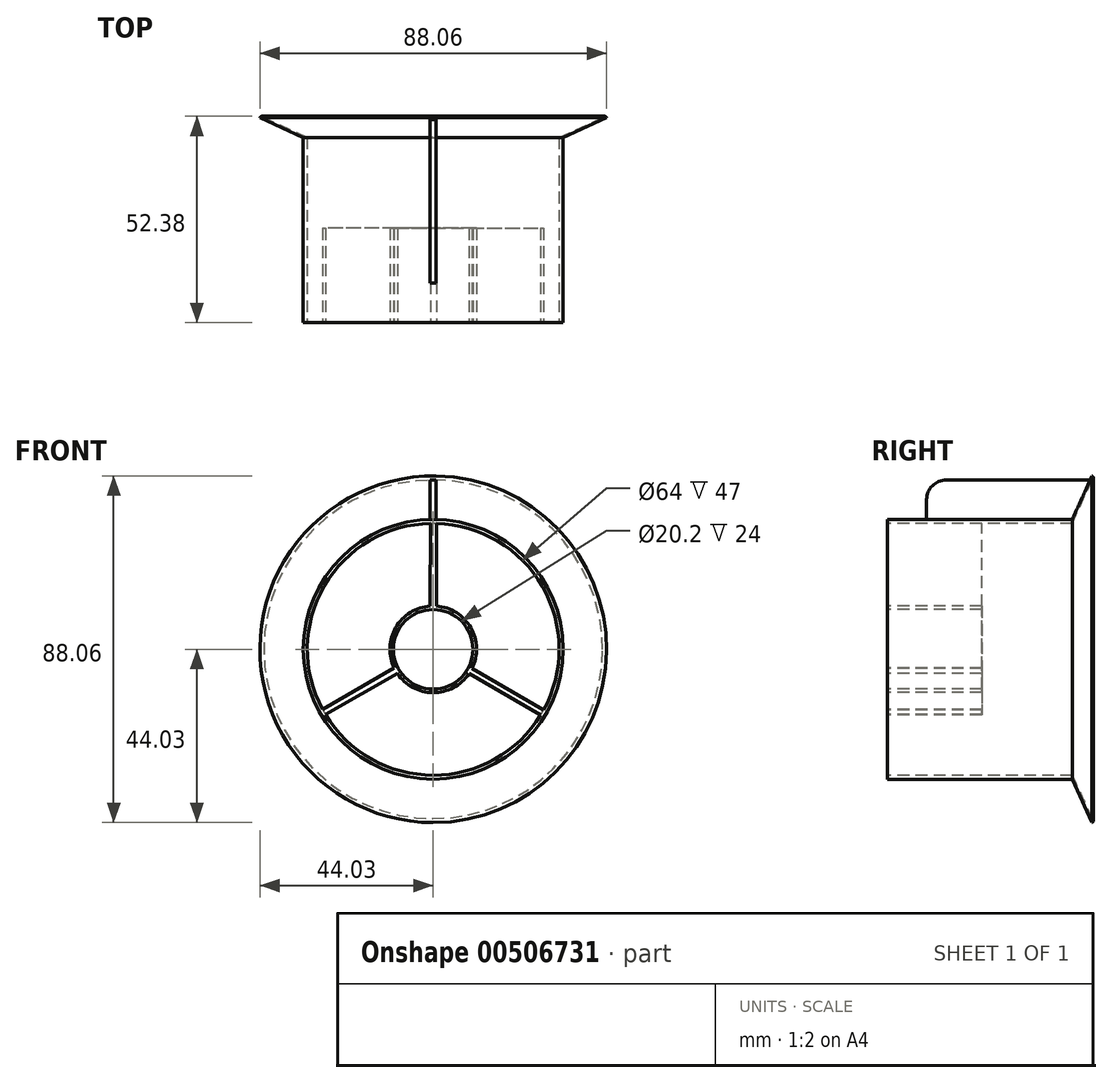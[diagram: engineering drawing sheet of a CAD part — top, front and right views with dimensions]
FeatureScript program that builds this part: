
annotation { "Feature Type Name" : "Feature", "Feature Type Description" : "" }
export const myFeature = defineFeature(function(context is Context, id is Id, definition is map)
    precondition{}
    {
        {
            var Q0;
            Q0=qCreatedBy(makeId("Front.planeOp"),FACE);
            var sketch = newSketch(context, id + "F0", { "sketchPlane" : qUnion([Q0])});
            skCircle(sketch, "E0", {"center": v(0, 0) * mm, "radius": 32 * mm});
            skCircle(sketch, "E1", {"center": v(0, 0) * mm, "radius": 33 * mm});
            skCircle(sketch, "E2", {"center": v(0, 0) * mm, "radius": 10.1 * mm});
            skCircle(sketch, "E3", {"center": v(0, 0) * mm, "radius": 11 * mm});
            skPoint(sketch, "E4.center", {"position": v(0, 0.01) * mm});
            skLineSegment(sketch, "E5.trimOffspring", {"start": v(-0.76, 10.07) * mm, "end": v(-0.65, 33) * mm});
            skLineSegment(sketch, "E6.trimOffspring", {"start": v(0.82, 10.07) * mm, "end": v(0.82, 32.99) * mm});
            skCircle(sketch, "E7", {"center": v(0, 0.01) * mm, "radius": 44 * mm});
            skCircle(sketch, "E8", {"center": v(0, 0.01) * mm, "radius": 3.42 * mm});
            skCircle(sketch, "E9", {"center": v(0, 0.01) * mm, "radius": 43 * mm});
            skLineSegment(sketch, "E10.1.0", {"start": v(-9.13, -4.32) * mm, "end": v(-28.98, -15.78) * mm});
            skLineSegment(sketch, "E10.1.1", {"start": v(-8.34, -5.7) * mm, "end": v(-28.25, -17.06) * mm});
            skLineSegment(sketch, "E10.2.0", {"start": v(8.3, -5.74) * mm, "end": v(28.16, -17.2) * mm});
            skLineSegment(sketch, "E10.2.1", {"start": v(9.1, -4.38) * mm, "end": v(28.9, -15.93) * mm});
            skSolve(sketch);
        }
        {
            var Q0;
            Q0=makeQuery(id+"F0.imprint","IMPRINT",FACE,{"disambiguationData":[TD([[makeQuery(id+"F0.imprint","IMPRINT",EDGE,{"derivedFrom":sQuery(id+"F0.wireOp",EDGE,"E1")}),1.0]])]});
            extrude(context, id + "F1", {"entities" : qUnion([Q0]), "oppositeDirection" : true, "depth" : 47 * mm, "offsetDistance" : 25 * mm});
        }
        {
            var Q0;
            Q0=qCreatedBy(makeId("Right.planeOp"),FACE);
            var sketch = newSketch(context, id + "F2", { "sketchPlane" : qUnion([Q0])});
            skLineSegment(sketch, "E11.0", {"start": v(47, 32) * mm, "end": v(47, 32) * mm});
            skLineSegment(sketch, "E11.1", {"start": v(47, -33) * mm, "end": v(47, 33) * mm});
            skLineSegment(sketch, "E12.0", {"start": v(0, -42.99) * mm, "end": v(0, 43.01) * mm});
            skLineSegment(sketch, "E12.1", {"start": v(0, -43.99) * mm, "end": v(0, 44.01) * mm});
            skLineSegment(sketch, "E13", {"start": v(47, 32) * mm, "end": v(47, 32.39) * mm});
            skLineSegment(sketch, "E14", {"start": v(47, 32) * mm, "end": v(52, 43.02) * mm});
            skLineSegment(sketch, "E15", {"start": v(47, 33) * mm, "end": v(52, 44.03) * mm});
            skArc(sketch, "E16", {"start": v(52, 43.02) * mm, "mid": v(52.38, 43.52) * mm, "end": v(52, 44.03) * mm});
            skLineSegment(sketch, "E17", {"start": v(47, 32) * mm, "end": v(47, 33) * mm});
            skLineSegment(sketch, "E18", {"start": v(27.15, 0) * mm, "end": v(34.99, 0) * mm, "construction": true});
            skLineSegment(sketch, "E19", {"start": v(47, 33) * mm, "end": v(42.98, 33) * mm, "construction": true});
            skSolve(sketch);
        }
        {
            var Q0;
            {var subQ0=sQuery(id+"F2.wireOp",EDGE,"E14");Q0=makeQuery(id+"F2.imprint","IMPRINT",FACE,{"disambiguationData":[TD([[makeQuery(id+"F2.imprint","IMPRINT",EDGE,{"derivedFrom":subQ0}),1.0]])]});}
            var Q1;
            Q1=sQuery(id+"F2.wireOp",EDGE,"E18");
            revolve(context, id + "F3", {"operationType" : NewBodyOperationType.ADD, "entities" : qUnion([Q0]), "axis" : qUnion([Q1]), "revolveType" : RevolveType.FULL});
        }
        {
            var Q0;
            {var subQ0=sQuery(id+"F0.wireOp",EDGE,"E0");Q0=makeQuery(id+"FlOwrdUnQid0o9V_1.boolean.opBoolean","MERGE",FACE,{"derivedFrom":[makeQuery(id+"F1.opExtrude","CAP_FACE",FACE,{"disambiguationData":[OSD([subQ0,sQuery(id+"F0.wireOp",EDGE,"E1"),sQuery(id+"F0.wireOp",EDGE,"09d8qYk8-wVlR-Syt2-LU9I-Puvoe7KKkESJ")])],"isStart":true}),makeQuery(id+"FlOwrdUnQid0o9V_1.opExtrude","CAP_FACE",FACE,{"disambiguationData":[OSD([subQ0,sQuery(id+"F0.wireOp",EDGE,"a5a1febd-64e9-4a83-98ac-cafd24b6d020.1.0"),sQuery(id+"F0.wireOp",EDGE,"a5a1febd-64e9-4a83-98ac-cafd24b6d020.1.1"),sQuery(id+"F0.wireOp",EDGE,"a5a1febd-64e9-4a83-98ac-cafd24b6d020.1.2")])],"isStart":true}),makeQuery(id+"FlOwrdUnQid0o9V_1.opExtrude","CAP_FACE",FACE,{"disambiguationData":[OSD([subQ0,sQuery(id+"F0.wireOp",EDGE,"a5a1febd-64e9-4a83-98ac-cafd24b6d020.2.0"),sQuery(id+"F0.wireOp",EDGE,"a5a1febd-64e9-4a83-98ac-cafd24b6d020.2.1"),sQuery(id+"F0.wireOp",EDGE,"a5a1febd-64e9-4a83-98ac-cafd24b6d020.2.2")])],"isStart":true})]});}
            cPlane(context, id + "F4", {"entities" : qUnion([Q0]), "cplaneType" : CPlaneType.OFFSET, "offset" : 10 * mm, "oppositeDirection" : true, "width" : 150 * mm, "height" : 150 * mm});
        }
        {
            var Q0;
            Q0=qCreatedBy(id+"F4.planeOp",FACE);
            var sketch = newSketch(context, id + "F5", { "sketchPlane" : qUnion([Q0])});
            skArc(sketch, "E20.0", {"start": v(0.75, 43) * mm, "mid": v(0, 43.01) * mm, "end": v(-0.75, 43) * mm});
            skArc(sketch, "E21.0", {"start": v(0.75, 33) * mm, "mid": v(0, 33) * mm, "end": v(-0.75, 33) * mm});
            skLineSegment(sketch, "E22", {"start": v(0, 33) * mm, "end": v(0, 43.01) * mm, "construction": true});
            skLineSegment(sketch, "E23", {"start": v(-0.75, 33) * mm, "end": v(-0.75, 43) * mm});
            skLineSegment(sketch, "E24", {"start": v(0.75, 33) * mm, "end": v(0.75, 43) * mm});
            skLineSegment(sketch, "E25", {"start": v(-13.05, 0) * mm, "end": v(18.36, 0) * mm, "construction": true});
            skArc(sketch, "E26.MirrorCS", {"start": v(0.75, -43) * mm, "mid": v(0, -43.01) * mm, "end": v(-0.75, -43) * mm});
            skArc(sketch, "E27.MirrorCS", {"start": v(0.75, -33) * mm, "mid": v(0, -33) * mm, "end": v(-0.75, -33) * mm});
            skLineSegment(sketch, "E28.MirrorCS", {"start": v(0.75, -33) * mm, "end": v(0.75, -43) * mm});
            skLineSegment(sketch, "E29.MirrorCS", {"start": v(0, -33) * mm, "end": v(0, -43.01) * mm, "construction": true});
            skLineSegment(sketch, "E30.MirrorCS", {"start": v(-0.75, -33) * mm, "end": v(-0.75, -43) * mm});
            skSolve(sketch);
        }
        {
            var Q0;
            Q0=makeQuery(id+"F5.imprint","IMPRINT",FACE,{"disambiguationData":[TD([[makeQuery(id+"F5.imprint","IMPRINT",EDGE,{"derivedFrom":sQuery(id+"F5.wireOp",EDGE,"E26.MirrorCS")}),-1.0]])]});
            var Q1;
            Q1=makeQuery(id+"F5.imprint","IMPRINT",FACE,{"disambiguationData":[TD([[makeQuery(id+"F5.imprint","IMPRINT",EDGE,{"derivedFrom":sQuery(id+"F5.wireOp",EDGE,"E20.0")}),1.0]])]});
            extrude(context, id + "F6", {"entities" : qUnion([Q0, Q1]), "operationType" : NewBodyOperationType.ADD, "endBound" : BoundingType.UP_TO_NEXT, "oppositeDirection" : true, "depth" : 25 * mm, "offsetDistance" : 25 * mm});
        }
        {
            var Q0;
            Q0=qCreatedBy(makeId("Right.planeOp"),FACE);
            var sketch = newSketch(context, id + "F7", { "sketchPlane" : qUnion([Q0])});
            skPoint(sketch, "E31.newPointA", {"position": v(10, 43) * mm});
            skPoint(sketch, "E31.newPointB", {"position": v(10, 43) * mm});
            skArc(sketch, "E31.filletArc", {"start": v(15, 43) * mm, "mid": v(11.46, 41.54) * mm, "end": v(10, 38) * mm});
            skLineSegment(sketch, "E32", {"start": v(15, 43) * mm, "end": v(10, 43) * mm});
            skPoint(sketch, "E33.1.start.orphan", {"position": v(51.54, 43) * mm});
            skPoint(sketch, "E33.0.start.orphan", {"position": v(10, 33) * mm});
            skLineSegment(sketch, "E34", {"start": v(10, 38) * mm, "end": v(10, 43) * mm});
            skLineSegment(sketch, "E35", {"start": v(0, 0) * mm, "end": v(24.92, 0) * mm, "construction": true});
            skPoint(sketch, "E36.MirrorP", {"position": v(10, -43) * mm});
            skLineSegment(sketch, "E37.MirrorCS", {"start": v(10, -38) * mm, "end": v(10, -43) * mm});
            skArc(sketch, "E38.MirrorCS", {"start": v(15, -43) * mm, "mid": v(11.46, -41.54) * mm, "end": v(10, -38) * mm});
            skLineSegment(sketch, "E39.MirrorCS", {"start": v(15, -43) * mm, "end": v(10, -43) * mm});
            skPoint(sketch, "E40.MirrorP", {"position": v(10, -33) * mm});
            skSolve(sketch);
        }
        {
            var Q0;
            Q0 = qSketchRegion(id + "F7", true);
            extrude(context, id + "F8", {"entities" : qUnion([Q0]), "operationType" : NewBodyOperationType.REMOVE, "endBound" : BoundingType.SYMMETRIC, "oppositeDirection" : true, "depth" : 5 * mm, "offsetDistance" : 25 * mm});
        }
        {
            var Q0;
            {var subQ0=sQuery(id+"F0.wireOp",EDGE,"E10.1.0");var subQ1=sQuery(id+"F0.wireOp",EDGE,"E0");var subQ2=makeQuery(id+"F0.imprint","INTERSECT",VERTEX,{"derivedFrom":[subQ1,subQ0]});Q0=makeQuery(id+"F0.imprint","IMPRINT",FACE,{"disambiguationData":[TD([[makeQuery(id+"F0.imprint","IMPRINT",EDGE,{"disambiguationData":[TD([[subQ2,-1.0]])],"derivedFrom":subQ1}),1.0]])]});}
            var Q1;
            {var subQ0=sQuery(id+"F0.wireOp",EDGE,"E5.trimOffspring");var subQ1=sQuery(id+"F0.wireOp",EDGE,"E2");var subQ2=makeQuery(id+"F0.imprint","INTERSECT",VERTEX,{"derivedFrom":[subQ1,subQ0]});Q1=makeQuery(id+"F0.imprint","IMPRINT",FACE,{"disambiguationData":[TD([[makeQuery(id+"F0.imprint","IMPRINT",EDGE,{"disambiguationData":[TD([[subQ2,-1.0]])],"derivedFrom":subQ1}),-1.0]])]});}
            var Q2;
            {var subQ0=sQuery(id+"F0.wireOp",EDGE,"E10.1.0");var subQ1=sQuery(id+"F0.wireOp",EDGE,"E2");var subQ2=makeQuery(id+"F0.imprint","INTERSECT",VERTEX,{"derivedFrom":[subQ1,subQ0]});Q2=makeQuery(id+"F0.imprint","IMPRINT",FACE,{"disambiguationData":[TD([[makeQuery(id+"F0.imprint","IMPRINT",EDGE,{"disambiguationData":[TD([[subQ2,-1.0]])],"derivedFrom":subQ1}),-1.0]])]});}
            var Q3;
            {var subQ0=sQuery(id+"F0.wireOp",EDGE,"E10.1.1");var subQ1=sQuery(id+"F0.wireOp",EDGE,"E2");var subQ2=makeQuery(id+"F0.imprint","INTERSECT",VERTEX,{"derivedFrom":[subQ1,subQ0]});Q3=makeQuery(id+"F0.imprint","IMPRINT",FACE,{"disambiguationData":[TD([[makeQuery(id+"F0.imprint","IMPRINT",EDGE,{"disambiguationData":[TD([[subQ2,-1.0]])],"derivedFrom":subQ1}),-1.0]])]});}
            var Q4;
            {var subQ0=sQuery(id+"F0.wireOp",EDGE,"E10.2.0");var subQ1=sQuery(id+"F0.wireOp",EDGE,"E2");var subQ2=makeQuery(id+"F0.imprint","INTERSECT",VERTEX,{"derivedFrom":[subQ1,subQ0]});Q4=makeQuery(id+"F0.imprint","IMPRINT",FACE,{"disambiguationData":[TD([[makeQuery(id+"F0.imprint","IMPRINT",EDGE,{"disambiguationData":[TD([[subQ2,-1.0]])],"derivedFrom":subQ1}),-1.0]])]});}
            var Q5;
            {var subQ0=sQuery(id+"F0.wireOp",EDGE,"E10.2.0");var subQ1=sQuery(id+"F0.wireOp",EDGE,"E0");var subQ2=makeQuery(id+"F0.imprint","INTERSECT",VERTEX,{"derivedFrom":[subQ1,subQ0]});Q5=makeQuery(id+"F0.imprint","IMPRINT",FACE,{"disambiguationData":[TD([[makeQuery(id+"F0.imprint","IMPRINT",EDGE,{"disambiguationData":[TD([[subQ2,-1.0]])],"derivedFrom":subQ1}),1.0]])]});}
            var Q6;
            {var subQ0=sQuery(id+"F0.wireOp",EDGE,"E6.trimOffspring");var subQ1=sQuery(id+"F0.wireOp",EDGE,"E2");var subQ2=makeQuery(id+"F0.imprint","INTERSECT",VERTEX,{"derivedFrom":[subQ1,subQ0]});Q6=makeQuery(id+"F0.imprint","IMPRINT",FACE,{"disambiguationData":[TD([[makeQuery(id+"F0.imprint","IMPRINT",EDGE,{"disambiguationData":[TD([[subQ2,1.0]])],"derivedFrom":subQ1}),-1.0]])]});}
            var Q7;
            {var subQ0=sQuery(id+"F0.wireOp",EDGE,"E5.trimOffspring");var subQ1=sQuery(id+"F0.wireOp",EDGE,"E2");var subQ2=makeQuery(id+"F0.imprint","INTERSECT",VERTEX,{"derivedFrom":[subQ1,subQ0]});Q7=makeQuery(id+"F0.imprint","IMPRINT",FACE,{"disambiguationData":[TD([[makeQuery(id+"F0.imprint","IMPRINT",EDGE,{"disambiguationData":[TD([[subQ2,1.0]])],"derivedFrom":subQ1}),-1.0]])]});}
            var Q8;
            {var subQ0=sQuery(id+"F0.wireOp",EDGE,"E5.trimOffspring");var subQ1=sQuery(id+"F0.wireOp",EDGE,"E0");var subQ2=makeQuery(id+"F0.imprint","INTERSECT",VERTEX,{"derivedFrom":[subQ1,subQ0]});Q8=makeQuery(id+"F0.imprint","IMPRINT",FACE,{"disambiguationData":[TD([[makeQuery(id+"F0.imprint","IMPRINT",EDGE,{"disambiguationData":[TD([[subQ2,1.0]])],"derivedFrom":subQ1}),1.0]])]});}
            extrude(context, id + "F9", {"entities" : qUnion([Q0, Q1, Q2, Q3, Q4, Q5, Q6, Q7, Q8]), "operationType" : NewBodyOperationType.ADD, "oppositeDirection" : true, "depth" : 24 * mm, "offsetDistance" : 25 * mm});
        }
    });
